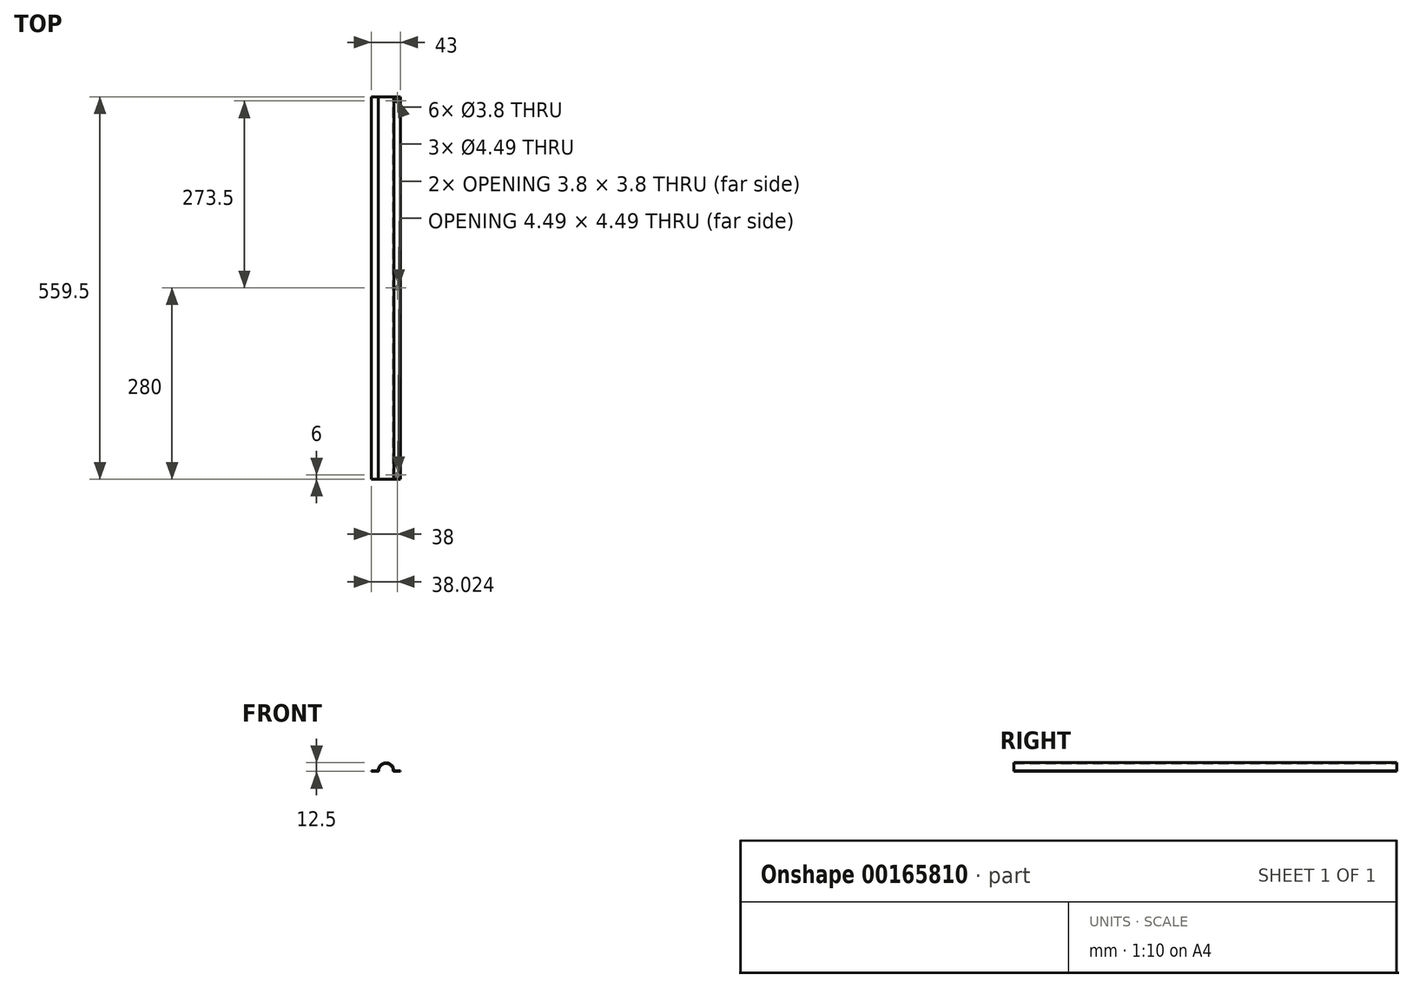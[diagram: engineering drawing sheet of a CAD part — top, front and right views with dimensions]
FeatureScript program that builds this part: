
annotation { "Feature Type Name" : "Feature", "Feature Type Description" : "" }
export const myFeature = defineFeature(function(context is Context, id is Id, definition is map)
    precondition{}
    {
        {
            var Q0;
            Q0=qCreatedBy(makeId("Front.planeOp"),FACE);
            var sketch = newSketch(context, id + "F0", { "sketchPlane" : qUnion([Q0])});
            skLineSegment(sketch, "E0.bottom", {"start": v(-10, -1) * mm, "end": v(10, -1) * mm, "construction": true});
            skLineSegment(sketch, "E0.top", {"start": v(-10, 1) * mm, "end": v(10, 1) * mm, "construction": true});
            skLineSegment(sketch, "E0.left", {"start": v(-10, -1) * mm, "end": v(-10, 1) * mm, "construction": true});
            skLineSegment(sketch, "E0.right", {"start": v(10, -1) * mm, "end": v(10, 1) * mm, "construction": true});
            skPoint(sketch, "E0.middle", {"position": v(0, 0) * mm});
            skLineSegment(sketch, "E1", {"start": v(-21.5, -1) * mm, "end": v(-11.55, -1) * mm});
            skPoint(sketch, "E2.start.orphan", {"position": v(0, 6.84) * mm});
            skPoint(sketch, "E3.MirrorCS.end.orphan", {"position": v(10.5, 1) * mm});
            skLineSegment(sketch, "E4.MirrorCS", {"start": v(21.5, -1) * mm, "end": v(10.5, -1) * mm});
            skLineSegment(sketch, "E5", {"start": v(-21.5, -1) * mm, "end": v(-21.5, 0) * mm});
            skLineSegment(sketch, "E6", {"start": v(-21.5, 0) * mm, "end": v(-11.5, 0) * mm});
            skPoint(sketch, "E7.orphan", {"position": v(-11.5, 0) * mm});
            skLineSegment(sketch, "E8.MirrorCS", {"start": v(21.5, -1) * mm, "end": v(11.55, -1) * mm});
            skLineSegment(sketch, "E9.MirrorCS", {"start": v(21.5, -1) * mm, "end": v(21.5, 0) * mm});
            skLineSegment(sketch, "E10.MirrorCS", {"start": v(21.5, 0) * mm, "end": v(11.5, 0) * mm});
            skPoint(sketch, "E11.end.orphan", {"position": v(0, 2.4) * mm});
            skLineSegment(sketch, "E12.bottom", {"start": v(-7.96, 1) * mm, "end": v(-6.5, 1) * mm, "construction": true});
            skLineSegment(sketch, "E12.top", {"start": v(-7.96, 5.2) * mm, "end": v(-6.5, 5.2) * mm, "construction": true});
            skLineSegment(sketch, "E12.left", {"start": v(-7.96, 1) * mm, "end": v(-7.96, 5.2) * mm, "construction": true});
            skLineSegment(sketch, "E12.right", {"start": v(-6.5, 1) * mm, "end": v(-6.5, 5.2) * mm, "construction": true});
            skLineSegment(sketch, "E13.bottom", {"start": v(-1.97, 2.6) * mm, "end": v(1.83, 2.6) * mm, "construction": true});
            skLineSegment(sketch, "E13.left", {"start": v(-1.97, 2.6) * mm, "end": v(-1.9, 1) * mm, "construction": true});
            skLineSegment(sketch, "E13.right", {"start": v(1.83, 2.6) * mm, "end": v(1.9, 1) * mm, "construction": true});
            skPoint(sketch, "E13.middle", {"position": v(0, 1) * mm});
            skPoint(sketch, "E13.top.start.orphan", {"position": v(-1.83, -0.6) * mm});
            skPoint(sketch, "E14.orphan", {"position": v(1.97, -0.6) * mm});
            skPoint(sketch, "E15.MirrorCS.start.orphan", {"position": v(10.5, -1) * mm});
            skArc(sketch, "E16", {"start": v(11.5, 0) * mm, "mid": v(0, 11.5) * mm, "end": v(-11.5, 0) * mm});
            skArc(sketch, "E17", {"start": v(10.55, 0) * mm, "mid": v(0, 10.55) * mm, "end": v(-10.55, 0) * mm});
            skPoint(sketch, "E18.visualSharp", {"position": v(-10.5, -1) * mm});
            skArc(sketch, "E18.filletArc", {"start": v(-11.55, -1) * mm, "mid": v(-10.84, -0.7) * mm, "end": v(-10.55, 0) * mm});
            skArc(sketch, "E19.filletArc", {"start": v(10.55, 0) * mm, "mid": v(10.84, -0.7) * mm, "end": v(11.55, -1) * mm});
            skSolve(sketch);
        }
        {
            var Q0;
            Q0 = qSketchRegion(id + "F0", true);
            var Q1;
            Q1 = qSketchRegion(id + "F2", true);
            extrude(context, id + "F1", {"entities" : qUnion([Q0, Q1]), "depth" : 559.5 * mm});
        }
        {
            var Q0;
            Q0=makeQuery(id+"F1.opExtrude","SWEPT_FACE",FACE,{"disambiguationData":[OSD([sQuery(id+"F0.wireOp",EDGE,"E10.MirrorCS")])]});
            var sketch = newSketch(context, id + "F2", { "sketchPlane" : qUnion([Q0])});
            skCircle(sketch, "E20", {"center": v(16.5, -279.5) * mm, "radius": 1.9 * mm});
            skCircle(sketch, "E21", {"center": v(16.5, -6) * mm, "radius": 1.9 * mm});
            skCircle(sketch, "E22", {"center": v(16.52, -553.5) * mm, "radius": 2.24 * mm});
            skLineSegment(sketch, "E23", {"start": v(16.5, 0) * mm, "end": v(16.5, -559.5) * mm, "construction": true});
            skSolve(sketch);
        }
        {
            var Q0;
            Q0 = qSketchRegion(id + "F2", true);
            extrude(context, id + "F3", {"entities" : qUnion([Q0]), "operationType" : NewBodyOperationType.REMOVE, "endBound" : BoundingType.UP_TO_NEXT, "oppositeDirection" : true, "depth" : 25 * mm});
        }
    });
